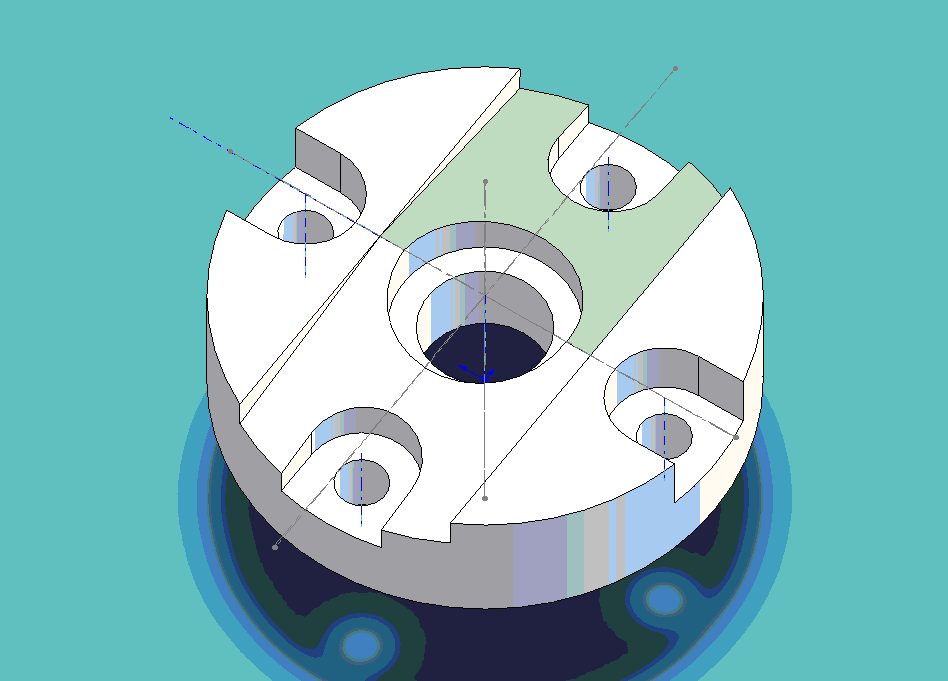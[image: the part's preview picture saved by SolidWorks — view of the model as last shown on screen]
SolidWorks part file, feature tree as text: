
SOLIDWORKS PART (.sldprt)
format: sldprt  version: not decoded by parser v0  size: 195,584 bytes
history: native  units: mm
features: sketch x9, cut_extrude x4, plane x3, material x1, extrude x1, cut_revolve x1, mirror x1, pattern_circular x1 (+10 scaffold rows collapsed)
feature tree (31):
  scaffold x10  (default folders/planes/origin — collapsed)
  material  "Nickel"
  plane  "Frontal"
  plane  "Horizontal"
  plane  "Profile"
  sketch  "Sketch1"  dims[D1=110.744mm]
  extrude  "Extrude1"  Depth=29.464mm
  sketch  "Sketch2"
  sketch  "Sketch3"
  sketch  "Sketch4"  dims[D3=27.432mm D1=25.4mm D2=25.4mm]
  cut_extrude  "Cut-Extrude1"  Depth=29.464mm
  sketch  "Sketch5"  dims[D1=39.116mm]
  cut_extrude  "Cut-Extrude2"  Depth=11.176mm
  sketch  "Sketch6"  dims[D1=50.8mm D2=25.4mm]
  cut_revolve  "Cut-Revolve1"  Angle=8deg
  mirror  "Mirror1"
  sketch  "Sketch9"  dims[c1.D1=~37.946082mm c1.D3=~44.753972mm c2.D1=24.13mm c2.D2=12.065mm c2.D3=~22.369394mm c3.D1=24.13mm c3.D2=12.065mm]
  cut_extrude  "Cut-Extrude4"  [1 undecoded]
  sketch  "Sketch12"  dims[D1=~4.84224mm]
  cut_extrude  "Cut-Extrude5"  [1 undecoded]
  sketch  "Sketch17"
  pattern_circular  "CirPattern1"  Count=4  [1 undecoded]
decode coverage: 11 of 17 modeling features carry decoded parameters
note: ~ marks probable driven/reference dimensions
note: 3 parameter values undecoded
note: suppression state not decoded; provenance and decode notes live in map.json
